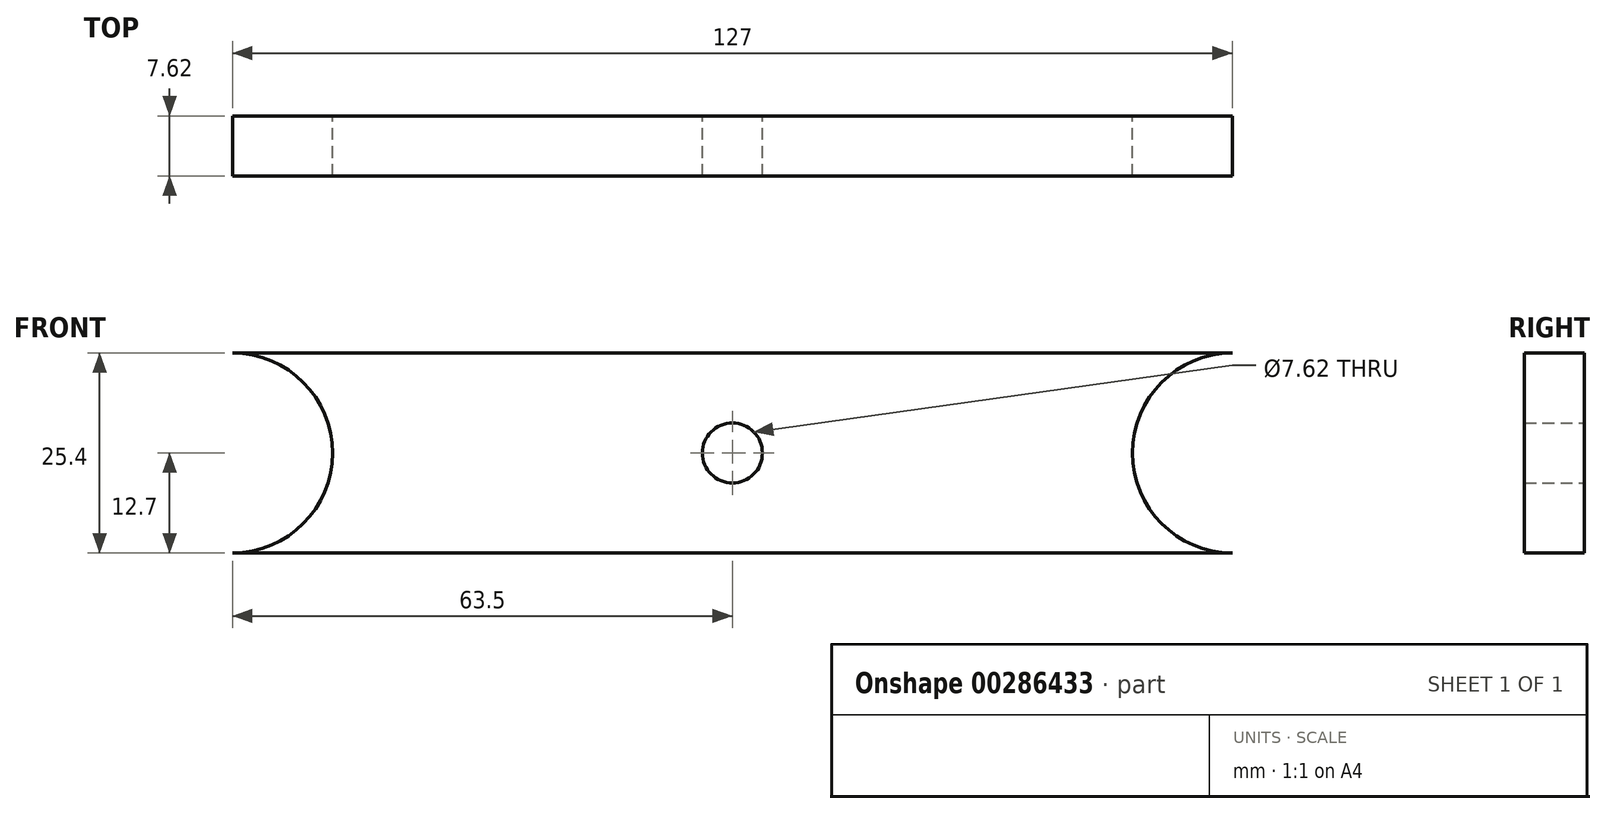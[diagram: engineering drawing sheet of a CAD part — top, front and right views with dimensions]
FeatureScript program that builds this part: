
annotation { "Feature Type Name" : "Feature", "Feature Type Description" : "" }
export const myFeature = defineFeature(function(context is Context, id is Id, definition is map)
    precondition{}
    {
        {
            var Q0;
            Q0=qCreatedBy(makeId("Front.planeOp"),FACE);
            var sketch = newSketch(context, id + "F0", { "sketchPlane" : qUnion([Q0])});
            skLineSegment(sketch, "E0.bottom", {"start": v(-63.5, -12.7) * mm, "end": v(63.5, -12.7) * mm});
            skLineSegment(sketch, "E0.top", {"start": v(-63.5, 12.7) * mm, "end": v(63.5, 12.7) * mm});
            skPoint(sketch, "E0.middle", {"position": v(0, 0) * mm});
            skArc(sketch, "E1", {"start": v(-63.5, -12.7) * mm, "mid": v(-50.8, 0) * mm, "end": v(-63.5, 12.7) * mm});
            skArc(sketch, "E2", {"start": v(63.5, 12.7) * mm, "mid": v(50.8, 0) * mm, "end": v(63.5, -12.7) * mm});
            skCircle(sketch, "E3", {"center": v(0, 0) * mm, "radius": 3.81 * mm});
            skSolve(sketch);
        }
        {
            var Q0;
            Q0 = qSketchRegion(id + "F0", true);
            extrude(context, id + "F1", {"entities" : qUnion([Q0]), "depth" : 7.62 * mm});
        }
    });
